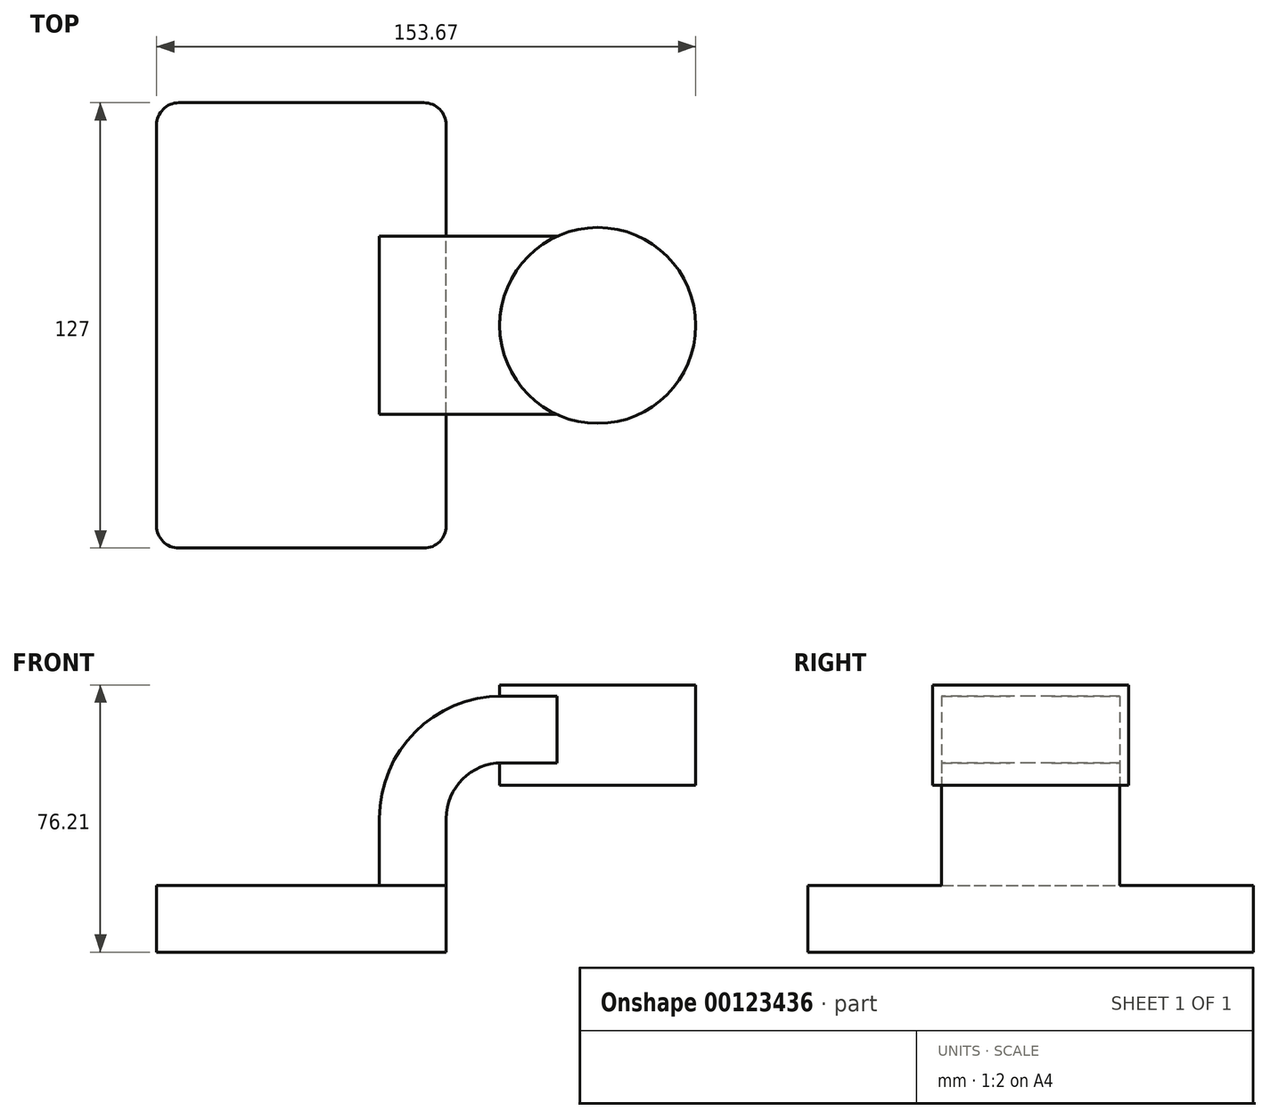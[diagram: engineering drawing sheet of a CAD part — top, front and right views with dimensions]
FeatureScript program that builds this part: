
annotation { "Feature Type Name" : "Feature", "Feature Type Description" : "" }
export const myFeature = defineFeature(function(context is Context, id is Id, definition is map)
    precondition{}
    {
        {
            var Q0;
            Q0=qCreatedBy(makeId("Front.planeOp"),FACE);
            var sketch = newSketch(context, id + "F0", { "sketchPlane" : qUnion([Q0])});
            skLineSegment(sketch, "E0.bottom", {"start": v(-41.27, -9.53) * mm, "end": v(41.28, -9.53) * mm});
            skLineSegment(sketch, "E0.top", {"start": v(-41.28, 9.53) * mm, "end": v(41.28, 9.53) * mm});
            skLineSegment(sketch, "E0.left", {"start": v(-41.28, -9.53) * mm, "end": v(-41.28, 9.53) * mm});
            skLineSegment(sketch, "E0.right", {"start": v(41.28, -9.53) * mm, "end": v(41.28, 9.52) * mm});
            skPoint(sketch, "E0.middle", {"position": v(0, 0) * mm});
            skLineSegment(sketch, "E1.bottom", {"start": v(61.6, 66.67) * mm, "end": v(112.4, 66.67) * mm});
            skLineSegment(sketch, "E1.top", {"start": v(61.6, 38.1) * mm, "end": v(112.4, 38.1) * mm});
            skLineSegment(sketch, "E1.left", {"start": v(61.6, 66.67) * mm, "end": v(61.6, 38.1) * mm});
            skLineSegment(sketch, "E1.right", {"start": v(112.4, 66.67) * mm, "end": v(112.4, 38.1) * mm});
            skPoint(sketch, "E1.middle", {"position": v(87, 52.39) * mm});
            skLineSegment(sketch, "E2", {"start": v(41.28, 9.52) * mm, "end": v(41.28, 28.58) * mm});
            skArc(sketch, "E3", {"start": v(41.27, 28.58) * mm, "mid": v(45.92, 39.8) * mm, "end": v(57.15, 44.45) * mm});
            skLineSegment(sketch, "E4", {"start": v(57.15, 44.45) * mm, "end": v(84.45, 44.45) * mm});
            skLineSegment(sketch, "E5.0", {"start": v(57.15, 63.5) * mm, "end": v(84.45, 63.5) * mm});
            skArc(sketch, "E5.1", {"start": v(22.22, 28.58) * mm, "mid": v(32.45, 53.27) * mm, "end": v(57.15, 63.5) * mm});
            skLineSegment(sketch, "E5.2", {"start": v(22.22, 9.52) * mm, "end": v(22.22, 28.58) * mm});
            skLineSegment(sketch, "E6", {"start": v(84.45, 38.1) * mm, "end": v(84.45, 66.67) * mm});
            skPoint(sketch, "E6.startSnap0", {"position": v(87, 38.1) * mm});
            skFitSpline(sketch, "E7", {"points": [v(-41.27, 9.53) * mm, v(57.15, 63.5) * mm], "startDerivative": vector(1.2, 90.82) * mm, "endDerivative": vector(147.7, -0.86) * mm});
            skSolve(sketch);
        }
        {
            var Q0;
            Q0=makeQuery(id+"F0.imprint","IMPRINT",FACE,{"disambiguationData":[TD([[makeQuery(id+"F0.imprint","IMPRINT",EDGE,{"derivedFrom":sQuery(id+"F0.wireOp",EDGE,"E0.bottom")}),1.0]])]});
            extrude(context, id + "F1", {"entities" : qUnion([Q0]), "endBound" : BoundingType.SYMMETRIC, "depth" : 127 * mm});
        }
        {
            var Q0;
            {var subQ1=sQuery(id+"F0.wireOp",EDGE,"E2");Q0=makeQuery(id+"F0.imprint","IMPRINT",FACE,{"disambiguationData":[TD([[makeQuery(id+"F0.imprint","IMPRINT",EDGE,{"derivedFrom":subQ1}),1.0]])]});}
            var Q1;
            {var subQ0=sQuery(id+"F0.wireOp",EDGE,"E5.0");var subQ1=sQuery(id+"F0.wireOp",EDGE,"E1.left");var subQ2=makeQuery(id+"F0.imprint","INTERSECT",VERTEX,{"derivedFrom":[subQ1,subQ0]});Q1=makeQuery(id+"F0.imprint","IMPRINT",FACE,{"disambiguationData":[TD([[makeQuery(id+"F0.imprint","IMPRINT",EDGE,{"disambiguationData":[TD([[subQ2,-1.0]])],"derivedFrom":subQ1}),1.0]])]});}
            extrude(context, id + "F2", {"entities" : qUnion([Q0, Q1]), "operationType" : NewBodyOperationType.ADD, "endBound" : BoundingType.SYMMETRIC, "depth" : 50.8 * mm});
        }
        {
            var Q0;
            Q0=makeQuery(id+"F0.imprint","IMPRINT",FACE,{"disambiguationData":[TD([[makeQuery(id+"F0.imprint","IMPRINT",EDGE,{"derivedFrom":sQuery(id+"F0.wireOp",EDGE,"E5.1")}),1.0]])]});
            extrude(context, id + "F3", {"entities" : qUnion([Q0]), "operationType" : NewBodyOperationType.ADD, "endBound" : BoundingType.SYMMETRIC, "depth" : 19.05 * mm});
        }
        {
            var Q0;
            {var subQ0=sQuery(id+"F0.wireOp",EDGE,"E1.right");Q0=makeQuery(id+"F0.imprint","IMPRINT",FACE,{"disambiguationData":[TD([[makeQuery(id+"F0.imprint","IMPRINT",EDGE,{"derivedFrom":subQ0}),-1.0]])]});}
            var Q1;
            Q1=sQuery(id+"F0.wireOp",EDGE,"E6");
            revolve(context, id + "F4", {"operationType" : NewBodyOperationType.ADD, "entities" : qUnion([Q0]), "axis" : qUnion([Q1]), "revolveType" : RevolveType.FULL});
        }
        {
            var Q0;
            Q0=makeQuery(id+"F1.opExtrude","CAP_EDGE",EDGE,{"disambiguationData":[OSD([sQuery(id+"F0.wireOp",EDGE,"E0.left")])],"isStart":false});
            var Q1;
            Q1=makeQuery(id+"F1.opExtrude","CAP_EDGE",EDGE,{"disambiguationData":[OSD([sQuery(id+"F0.wireOp",EDGE,"E0.right")])],"isStart":false});
            var Q2;
            Q2=makeQuery(id+"F1.opExtrude","CAP_EDGE",EDGE,{"disambiguationData":[OSD([sQuery(id+"F0.wireOp",EDGE,"E0.right")])],"isStart":true});
            var Q3;
            Q3=makeQuery(id+"F1.opExtrude","CAP_EDGE",EDGE,{"disambiguationData":[OSD([sQuery(id+"F0.wireOp",EDGE,"E0.left")])],"isStart":true});
            fillet(context, id + "F5", {"entities" : qUnion([Q0, Q1, Q2, Q3]), "radius" : 6.35 * mm, "tangentPropagation" : true, "allowEdgeOverflow" : false});
        }
    });
